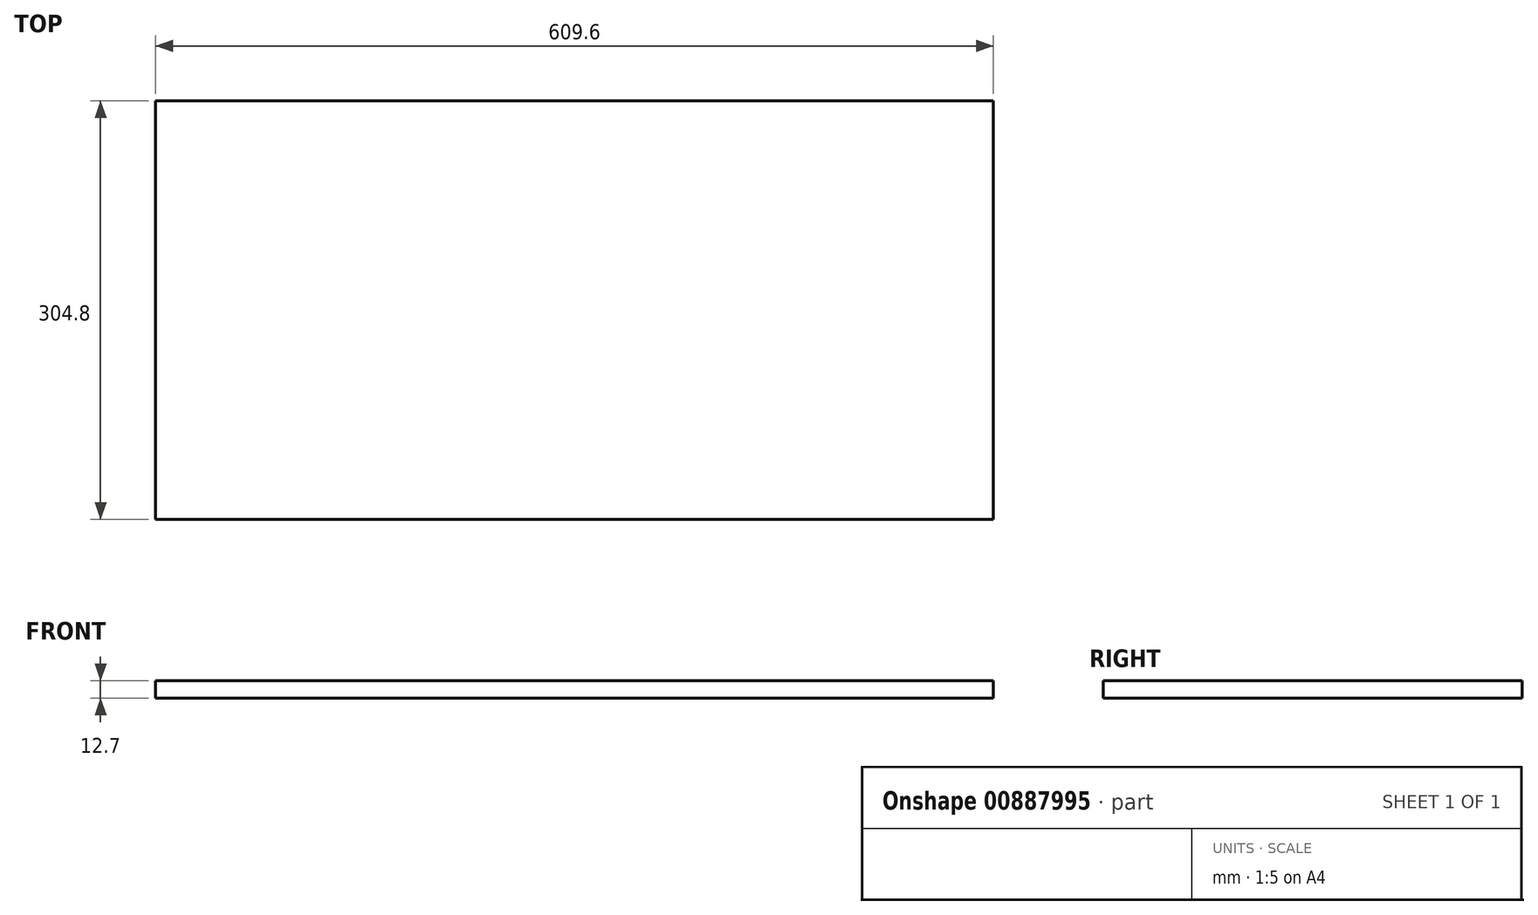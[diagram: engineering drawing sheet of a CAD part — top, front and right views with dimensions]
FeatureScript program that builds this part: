
annotation { "Feature Type Name" : "Feature", "Feature Type Description" : "" }
export const myFeature = defineFeature(function(context is Context, id is Id, definition is map)
    precondition{}
    {
        {
            var Q0;
            Q0=qCreatedBy(makeId("Top.planeOp"),FACE);
            var sketch = newSketch(context, id + "F0", { "sketchPlane" : qUnion([Q0])});
            skLineSegment(sketch, "E0.bottom", {"start": v(304.8, -152.4) * mm, "end": v(-304.8, -152.4) * mm});
            skLineSegment(sketch, "E0.top", {"start": v(304.8, 152.4) * mm, "end": v(-304.8, 152.4) * mm});
            skLineSegment(sketch, "E0.left", {"start": v(304.8, -152.4) * mm, "end": v(304.8, 152.4) * mm});
            skLineSegment(sketch, "E0.right", {"start": v(-304.8, -152.4) * mm, "end": v(-304.8, 152.4) * mm});
            skPoint(sketch, "E0.middle", {"position": v(0, 0) * mm});
            skSolve(sketch);
        }
        {
            var Q0;
            Q0=makeQuery(id+"F0.imprint","IMPRINT",FACE,{"disambiguationData":[TD([[makeQuery(id+"F0.imprint","IMPRINT",EDGE,{"derivedFrom":sQuery(id+"F0.wireOp",EDGE,"E0.bottom")}),-1.0]])]});
            extrude(context, id + "F1", {"entities" : qUnion([Q0]), "depth" : 12.7 * mm, "offsetDistance" : 25.4 * mm});
        }
    });
